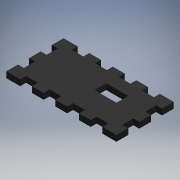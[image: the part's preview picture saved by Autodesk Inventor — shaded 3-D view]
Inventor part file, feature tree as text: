
AUTODESK INVENTOR PART (.ipt)
format: ipt  version: 2019 (Build 230136000, 136)  size: 179,200 bytes
history: native  units: mm
features: extrude x2, sketch x2
ambient origin geometry x8: Origin, YZ Plane, XZ Plane, XY Plane, X Axis, Y Axis, Z Axis, Center Point
bodies: Solid1 (feature_tree)
feature tree (4):
  extrude  "Extrusion1"  Depth=39.0mm
  extrude  "Extrusion2"  Depth=4.0mm
  sketch  "Sketch1"  dims[d0=75.0mm d1=39.0mm]
  sketch  "Sketch2"  dims[d10=4.0mm d11=0.0mm d12=4.0mm d13=4.0mm d14=8.0mm d15=8.0mm d16=8.0mm d17=8.0mm d18=4.0mm d19=4.0mm d20=0.0mm d21=15.0mm d22=19.0mm d23=8.0mm d24=19.0mm]
